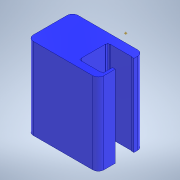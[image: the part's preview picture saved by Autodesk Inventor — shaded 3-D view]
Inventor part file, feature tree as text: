
AUTODESK INVENTOR PART (.ipt)
format: ipt  version: 2022 (Build 260153000, 153)  size: 229,888 bytes
history: native  units: mm
features: extrude x7, sketch x6, hole x2, projected_geometry x2, plane x1, thicken_offset x1, fillet x1
ambient origin geometry x8: Origin, YZ Plane, XZ Plane, XY Plane, X Axis, Y Axis, Z Axis, Center Point
bodies: Solid1 (feature_tree)
feature tree (20):
  extrude  "Extrusion1"  Depth=44.0mm TaperAngle=0.0deg
  sketch  "Sketch2"  dims[d3=44.0mm d4=35.0mm d5=0.0mm]
  extrude  "Extrusion2"  Depth=10.0mm
  hole  "Hole2"  [1 undecoded]
  plane  "Work Plane1"
  extrude  "Extrusion6"  Depth=5.0mm TaperAngle=0.0deg
  thicken_offset  "Thicken1"
  extrude  "Extrusion7"  Depth=3.0mm
  extrude  "Extrusion8"  Depth=3.0mm
  hole  "Hole3"  [1 undecoded]
  extrude  "Extrusion9"  Depth=3.0mm
  extrude  "Extrusion10"  Depth=3.0mm
  fillet  "Fillet1"  Radius=1.0mm
  sketch  "Sketch6"  dims[d6=10.0mm d7=10.0mm]
  projected_geometry  "Projected Loop2"
  sketch  "Sketch7"  dims[d8=16.6mm d9=0.0mm]
  sketch  "Sketch8"  dims[d20=4.0mm d21=6.0mm d22=4.0mm d23=2.0mm d24=90.0deg d25=10.0mm d26=0.0mm d30=4.0mm]
  sketch  "Sketch10"  dims[d40=4.0mm d41=5.0mm d42=0.0mm]
  sketch  "Sketch11"  dims[d43=0.1mm d44=0.1mm d45=1.0mm d46=1.0mm d47=0.2mm d48=0.2mm d49=1.0mm d50=1.0mm d51=0.2mm d52=0.0mm d53=0.0mm d54=1.5mm d55=10.0mm d56=0.0mm d57=24.03mm d59=8.5mm d60=10.0mm d61=9.382mm d62=22.0mm d63=4.0mm d64=6.0mm d65=6.3mm d66=2.0mm d67=90.0deg d68=10.0mm d69=0.0mm d70=5.0mm d71=5.0mm d72=5.0mm d73=4.0mm d74=0.0mm d75=0.0mm d76=0.0mm d77=0.0mm d78=3.0mm]
  projected_geometry  "Projected Loop3"
note: 2 required parameter values undecoded (feature->parameter linkage not recoverable at this tier; creation-order binding heuristic only, values carry confidence <= 0.55)
